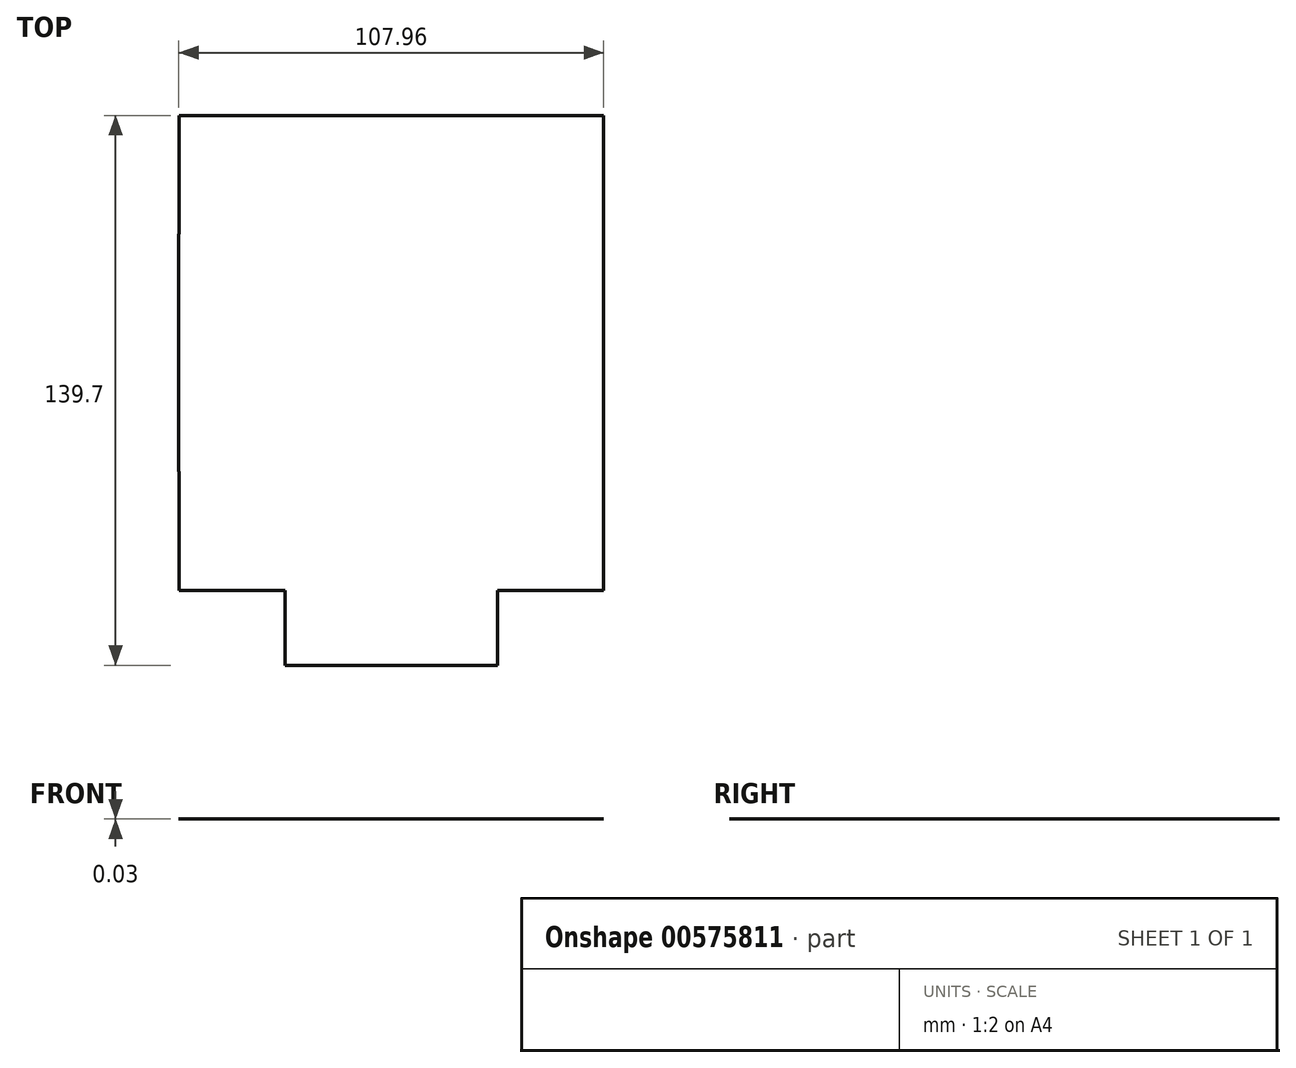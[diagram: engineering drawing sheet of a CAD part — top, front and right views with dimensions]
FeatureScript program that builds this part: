
annotation { "Feature Type Name" : "Feature", "Feature Type Description" : "" }
export const myFeature = defineFeature(function(context is Context, id is Id, definition is map)
    precondition{}
    {
        {
            var Q0;
            Q0=qCreatedBy(makeId("Top.planeOp"),FACE);
            var sketch = newSketch(context, id + "F0", { "sketchPlane" : qUnion([Q0])});
            skLineSegment(sketch, "E0.bottom", {"start": v(53.98, 60.33) * mm, "end": v(-53.98, 60.33) * mm});
            skLineSegment(sketch, "E0.top", {"start": v(53.97, -60.32) * mm, "end": v(-53.98, -60.32) * mm});
            skLineSegment(sketch, "E0.left", {"start": v(53.98, 60.33) * mm, "end": v(53.97, -60.32) * mm});
            skLineSegment(sketch, "E0.right", {"start": v(-53.98, 60.33) * mm, "end": v(-53.98, -60.32) * mm});
            skPoint(sketch, "E0.middle", {"position": v(0, 0) * mm});
            skPoint(sketch, "E1.middle", {"position": v(0, -60.32) * mm});
            skLineSegment(sketch, "E2.bottom", {"start": v(26.99, -41.27) * mm, "end": v(-26.99, -41.27) * mm});
            skLineSegment(sketch, "E2.top", {"start": v(26.99, -79.37) * mm, "end": v(-26.99, -79.37) * mm});
            skLineSegment(sketch, "E2.left", {"start": v(26.99, -41.27) * mm, "end": v(26.99, -79.37) * mm});
            skLineSegment(sketch, "E2.right", {"start": v(-26.99, -41.27) * mm, "end": v(-26.99, -79.37) * mm});
            skSolve(sketch);
        }
        {
            var Q0;
            Q0 = qSketchRegion(id + "F0", true);
            extrude(context, id + "F1", {"entities" : qUnion([Q0]), "depth" : 3 / 101.6 * mm, "offsetDistance" : 25.4 * mm});
        }
        {
            var Q0;
            Q0=makeQuery(id+"F1.opExtrude","SWEPT_FACE",FACE,{"disambiguationData":[OSD([sQuery(id+"F0.wireOp",EDGE,"E0.left")])]});
            var sketch = newSketch(context, id + "F2", { "sketchPlane" : qUnion([Q0])});
            skLineSegment(sketch, "E3", {"start": v(0, 0) * mm, "end": v(0, 19.05) * mm, "construction": true});
            skLineSegment(sketch, "E4.bottom", {"start": v(30.16, 19.05) * mm, "end": v(-30.16, 19.05) * mm});
            skLineSegment(sketch, "E4.top", {"start": v(30.16, 0) * mm, "end": v(-30.16, 0) * mm});
            skLineSegment(sketch, "E4.left", {"start": v(30.16, 19.05) * mm, "end": v(30.16, 0) * mm});
            skLineSegment(sketch, "E4.right", {"start": v(-30.16, 19.05) * mm, "end": v(-30.16, 0) * mm});
            skPoint(sketch, "E4.middle", {"position": v(0, 9.53) * mm});
            skSolve(sketch);
        }
        {
            var Q0;
            Q0=makeQuery(id+"F2.imprint","IMPRINT",FACE,{"disambiguationData":[TD([[makeQuery(id+"F2.imprint","IMPRINT",EDGE,{"derivedFrom":sQuery(id+"F2.wireOp",EDGE,"E4.bottom")}),1.0]])]});
            extrude(context, id + "F3", {"entities" : qUnion([Q0]), "operationType" : NewBodyOperationType.REMOVE, "oppositeDirection" : true, "depth" : 3 / 101.6 * mm, "offsetDistance" : 25.4 * mm});
        }
        {
            var Q0;
            Q0=makeQuery(id+"F1.opExtrude","SWEPT_FACE",FACE,{"disambiguationData":[OSD([sQuery(id+"F0.wireOp",EDGE,"E0.right")])]});
            var sketch = newSketch(context, id + "F4", { "sketchPlane" : qUnion([Q0])});
            skLineSegment(sketch, "E5", {"start": v(0, 0) * mm, "end": v(0, 19.05) * mm, "construction": true});
            skLineSegment(sketch, "E6.bottom", {"start": v(30.16, 19.05) * mm, "end": v(-30.16, 19.05) * mm});
            skLineSegment(sketch, "E6.top", {"start": v(30.16, 0) * mm, "end": v(-30.16, 0) * mm});
            skLineSegment(sketch, "E6.left", {"start": v(30.16, 19.05) * mm, "end": v(30.16, 0) * mm});
            skLineSegment(sketch, "E6.right", {"start": v(-30.16, 19.05) * mm, "end": v(-30.16, 0) * mm});
            skPoint(sketch, "E6.middle", {"position": v(0, 9.53) * mm});
            skSolve(sketch);
        }
        {
            var Q0;
            {var subQ0=sQuery(id+"F4.wireOp",EDGE,"E6.right");Q0=makeQuery(id+"F4.imprint","IMPRINT",FACE,{"disambiguationData":[TD([[makeQuery(id+"F4.imprint","IMPRINT",EDGE,{"derivedFrom":subQ0}),-1.0]])]});}
            var Q1;
            {var subQ0=sQuery(id+"F4.wireOp",EDGE,"E6.left");Q1=makeQuery(id+"F4.imprint","IMPRINT",FACE,{"disambiguationData":[TD([[makeQuery(id+"F4.imprint","IMPRINT",EDGE,{"derivedFrom":subQ0}),1.0]])]});}
            extrude(context, id + "F5", {"entities" : qUnion([Q0, Q1]), "operationType" : NewBodyOperationType.REMOVE, "oppositeDirection" : true, "depth" : 3 / 101.6 * mm, "offsetDistance" : 25.4 * mm});
        }
    });
